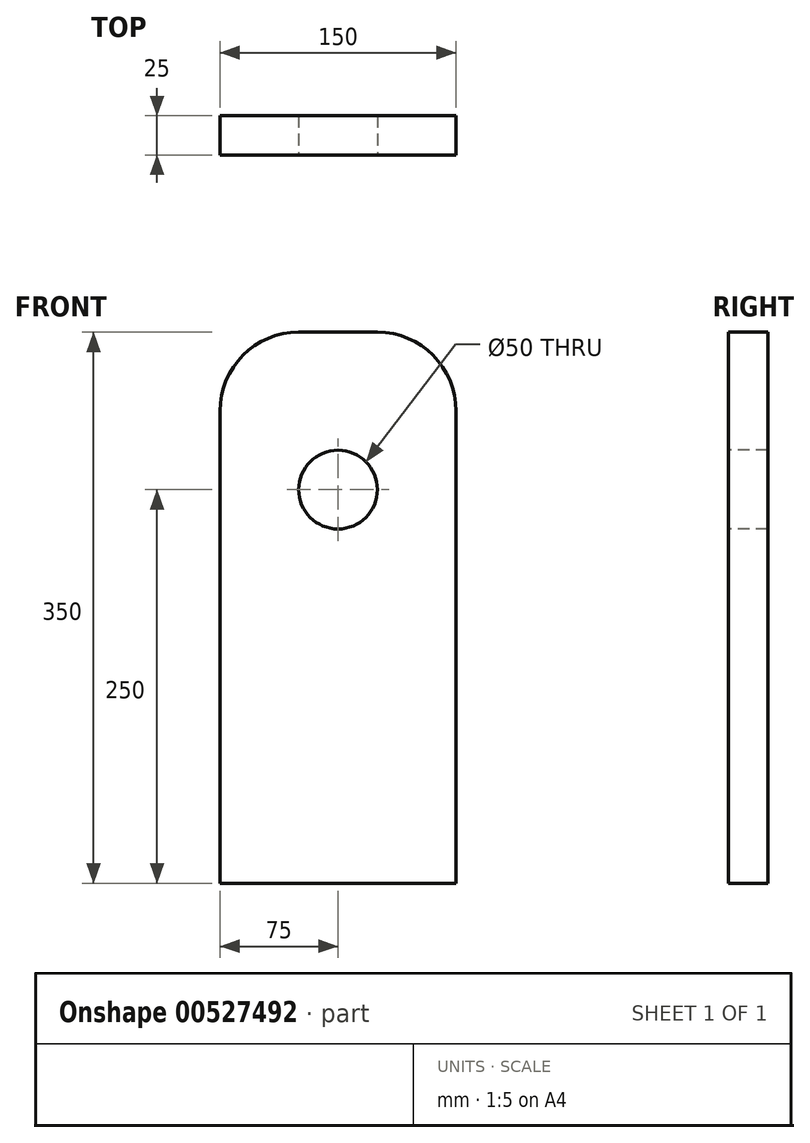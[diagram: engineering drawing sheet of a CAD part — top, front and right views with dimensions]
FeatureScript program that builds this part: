
annotation { "Feature Type Name" : "Feature", "Feature Type Description" : "" }
export const myFeature = defineFeature(function(context is Context, id is Id, definition is map)
    precondition{}
    {
        {
            var Q0;
            Q0=qCreatedBy(makeId("Front.planeOp"),FACE);
            var sketch = newSketch(context, id + "F0", { "sketchPlane" : qUnion([Q0])});
            skLineSegment(sketch, "E0.bottom", {"start": v(169, 350) * mm, "end": v(19, 350) * mm});
            skLineSegment(sketch, "E0.top", {"start": v(169, 0) * mm, "end": v(19, 0) * mm});
            skLineSegment(sketch, "E0.left", {"start": v(169, 350) * mm, "end": v(169, 0) * mm});
            skLineSegment(sketch, "E0.right", {"start": v(19, 350) * mm, "end": v(19, 0) * mm});
            skSolve(sketch);
        }
        {
            var Q0;
            Q0 = qSketchRegion(id + "F0", true);
            extrude(context, id + "F1", {"entities" : qUnion([Q0]), "depth" : 25 * mm, "offsetDistance" : 25 * mm});
        }
        {
            var Q0;
            Q0=makeQuery(id+"F1.opExtrude","SWEPT_EDGE",EDGE,{"disambiguationData":[OSD([sQuery(id+"F0.wireOp",EDGE,"E0.bottom"),sQuery(id+"F0.wireOp",EDGE,"E0.right")])]});
            var Q1;
            Q1=makeQuery(id+"F1.opExtrude","SWEPT_EDGE",EDGE,{"disambiguationData":[OSD([sQuery(id+"F0.wireOp",EDGE,"E0.bottom"),sQuery(id+"F0.wireOp",EDGE,"E0.left")])]});
            fillet(context, id + "F2", {"entities" : qUnion([Q0, Q1]), "radius" : 50 * mm, "tangentPropagation" : true, "allowEdgeOverflow" : false});
        }
        {
            var Q0;
            Q0=makeQuery(id+"F1.opExtrude","CAP_FACE",FACE,{"disambiguationData":[OSD([sQuery(id+"F0.wireOp",EDGE,"E0.bottom"),sQuery(id+"F0.wireOp",EDGE,"E0.top"),sQuery(id+"F0.wireOp",EDGE,"E0.left"),sQuery(id+"F0.wireOp",EDGE,"E0.right")])],"isStart":false});
            var sketch = newSketch(context, id + "F3", { "sketchPlane" : qUnion([Q0])});
            skLineSegment(sketch, "E1", {"start": v(94, 350) * mm, "end": v(94, 0) * mm, "construction": true});
            skCircle(sketch, "E2", {"center": v(94, 250) * mm, "radius": 19.98 * mm, "construction": true});
            skSolve(sketch);
        }
        {
            var Q0;
            Q0=sQuery(id+"F3.wireOp",VERTEX,"E2.center");
            var Q1;
            Q1=makeQuery(id+"F1.opExtrude","SWEPT_BODY",BODY,{"disambiguationData":[OSD([sQuery(id+"F0.wireOp",EDGE,"E0.bottom"),sQuery(id+"F0.wireOp",EDGE,"E0.top"),sQuery(id+"F0.wireOp",EDGE,"E0.left"),sQuery(id+"F0.wireOp",EDGE,"E0.right")])]});
            hole(context, id + "F4", {"style" : HoleStyle.SIMPLE, "endStyle" : HoleEndStyle.THROUGH, "holeDiameter" : 50 * mm, "isTappedThrough" : true, "tappedDepth" : 12 * mm, "tapClearance" : 3, "locations" : qUnion([Q0]), "scope" : qUnion([Q1])});
        }
    });
